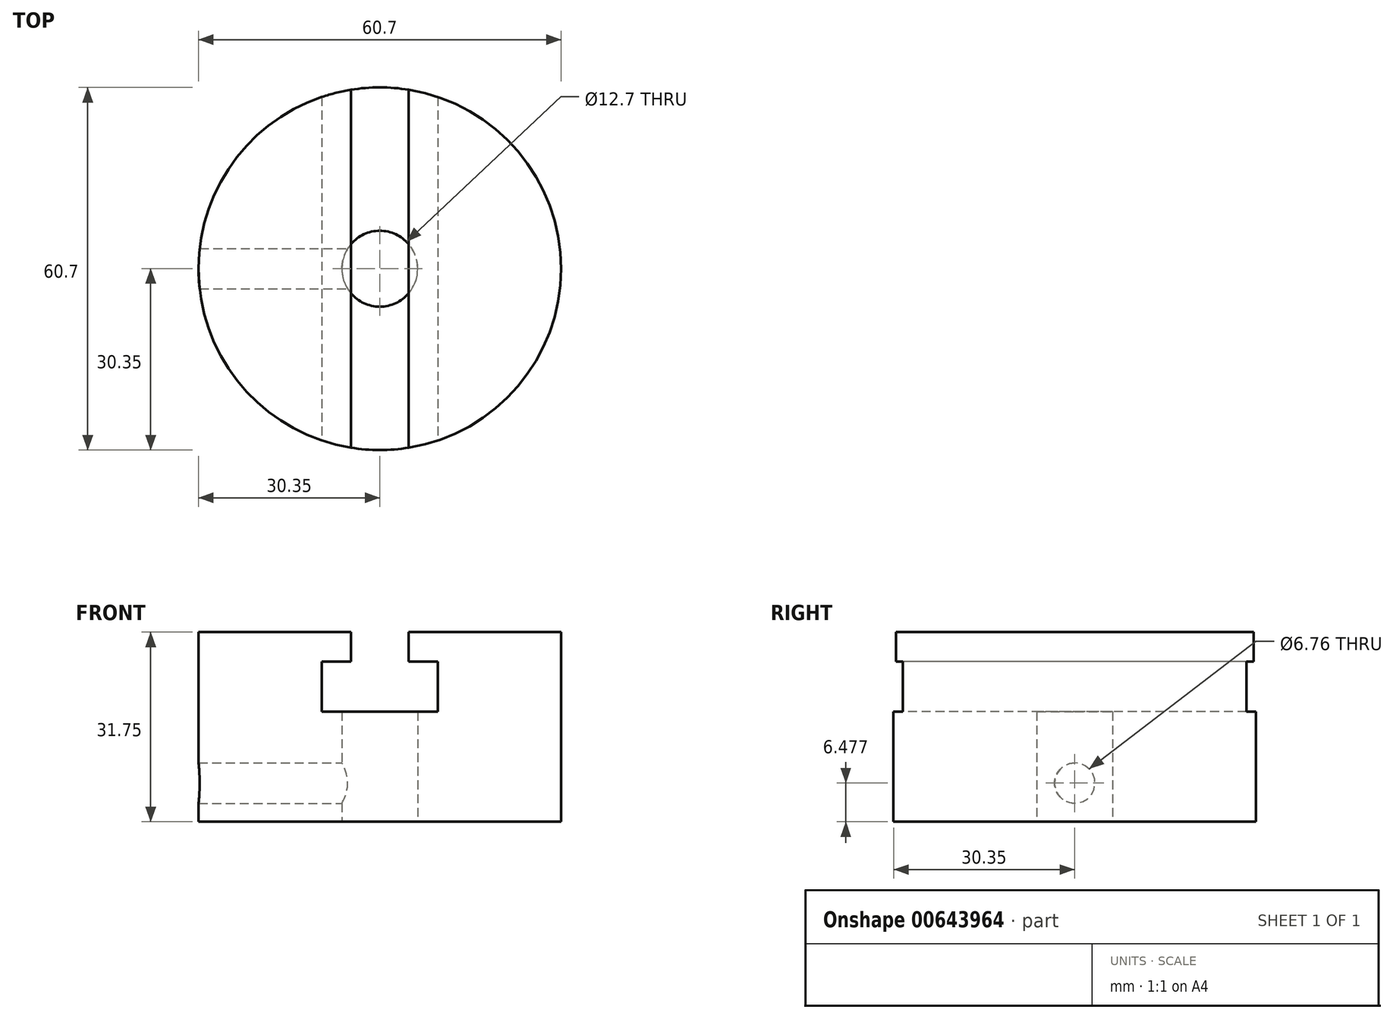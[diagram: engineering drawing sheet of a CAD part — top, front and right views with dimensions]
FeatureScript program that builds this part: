
annotation { "Feature Type Name" : "Feature", "Feature Type Description" : "" }
export const myFeature = defineFeature(function(context is Context, id is Id, definition is map)
    precondition{}
    {
        {
            var Q0;
            Q0=qCreatedBy(makeId("Top.planeOp"),FACE);
            var sketch = newSketch(context, id + "F0", { "sketchPlane" : qUnion([Q0])});
            skCircle(sketch, "E0", {"center": v(0, 0) * mm, "radius": 30.35 * mm});
            skSolve(sketch);
        }
        {
            var Q0;
            Q0=makeQuery(id+"F0.imprint","IMPRINT",FACE,{"disambiguationData":[TD([[makeQuery(id+"F0.imprint","IMPRINT",EDGE,{"derivedFrom":sQuery(id+"F0.wireOp",EDGE,"E0")}),1.0]])]});
            extrude(context, id + "F1", {"entities" : qUnion([Q0]), "depth" : 31.75 * mm, "offsetDistance" : 25.4 * mm});
        }
        {
            var Q0;
            Q0=makeQuery(id+"F1.opExtrude","CAP_FACE",FACE,{"disambiguationData":[OSD([sQuery(id+"F0.wireOp",EDGE,"E0")])],"isStart":true});
            var sketch = newSketch(context, id + "F2", { "sketchPlane" : qUnion([Q0])});
            skCircle(sketch, "E1", {"center": v(0, 0) * mm, "radius": 6.35 * mm});
            skSolve(sketch);
        }
        {
            var Q0;
            Q0=makeQuery(id+"F2.imprint","IMPRINT",FACE,{"disambiguationData":[TD([[makeQuery(id+"F2.imprint","IMPRINT",EDGE,{"derivedFrom":sQuery(id+"F2.wireOp",EDGE,"E1")}),1.0]])]});
            extrude(context, id + "F3", {"entities" : qUnion([Q0]), "operationType" : NewBodyOperationType.REMOVE, "oppositeDirection" : true, "depth" : 18.41 * mm, "offsetDistance" : 25.4 * mm});
        }
        {
            var Q0;
            Q0=qCreatedBy(makeId("Front.planeOp"),FACE);
            var sketch = newSketch(context, id + "F4", { "sketchPlane" : qUnion([Q0])});
            skLineSegment(sketch, "E2.bottom", {"start": v(-9.7, 26.8) * mm, "end": v(9.7, 26.8) * mm});
            skLineSegment(sketch, "E2.top", {"start": v(-9.7, 18.41) * mm, "end": v(9.7, 18.41) * mm});
            skLineSegment(sketch, "E2.left", {"start": v(-9.7, 26.8) * mm, "end": v(-9.7, 18.41) * mm});
            skLineSegment(sketch, "E2.right", {"start": v(9.7, 26.8) * mm, "end": v(9.7, 18.41) * mm});
            skLineSegment(sketch, "E3.bottom", {"start": v(4.83, 26.8) * mm, "end": v(-4.83, 26.8) * mm});
            skLineSegment(sketch, "E3.top", {"start": v(4.83, 33.35) * mm, "end": v(-4.83, 33.35) * mm});
            skLineSegment(sketch, "E3.left", {"start": v(4.83, 26.8) * mm, "end": v(4.83, 33.35) * mm});
            skLineSegment(sketch, "E3.right", {"start": v(-4.83, 26.8) * mm, "end": v(-4.83, 33.35) * mm});
            skSolve(sketch);
        }
        {
            var Q0;
            Q0 = qSketchRegion(id + "F4", true);
            extrude(context, id + "F5", {"entities" : qUnion([Q0]), "operationType" : NewBodyOperationType.REMOVE, "endBound" : BoundingType.SYMMETRIC, "oppositeDirection" : true, "depth" : 60.7 * mm, "offsetDistance" : 25.4 * mm});
        }
        {
            var Q0;
            Q0=qCreatedBy(makeId("Right.planeOp"),FACE);
            var sketch = newSketch(context, id + "F6", { "sketchPlane" : qUnion([Q0])});
            skCircle(sketch, "E4", {"center": v(0, 6.48) * mm, "radius": 3.38 * mm});
            skSolve(sketch);
        }
        {
            var Q0;
            Q0 = qSketchRegion(id + "F6", true);
            var Q1;
            Q1=sQuery(id+"F6.wireOp",EDGE,"E4");
            extrude(context, id + "F7", {"entities" : qUnion([Q0]), "operationType" : NewBodyOperationType.REMOVE, "surfaceEntities" : qUnion([Q1]), "oppositeDirection" : true, "depth" : 60.7 * mm, "offsetDistance" : 25.4 * mm});
        }
    });
